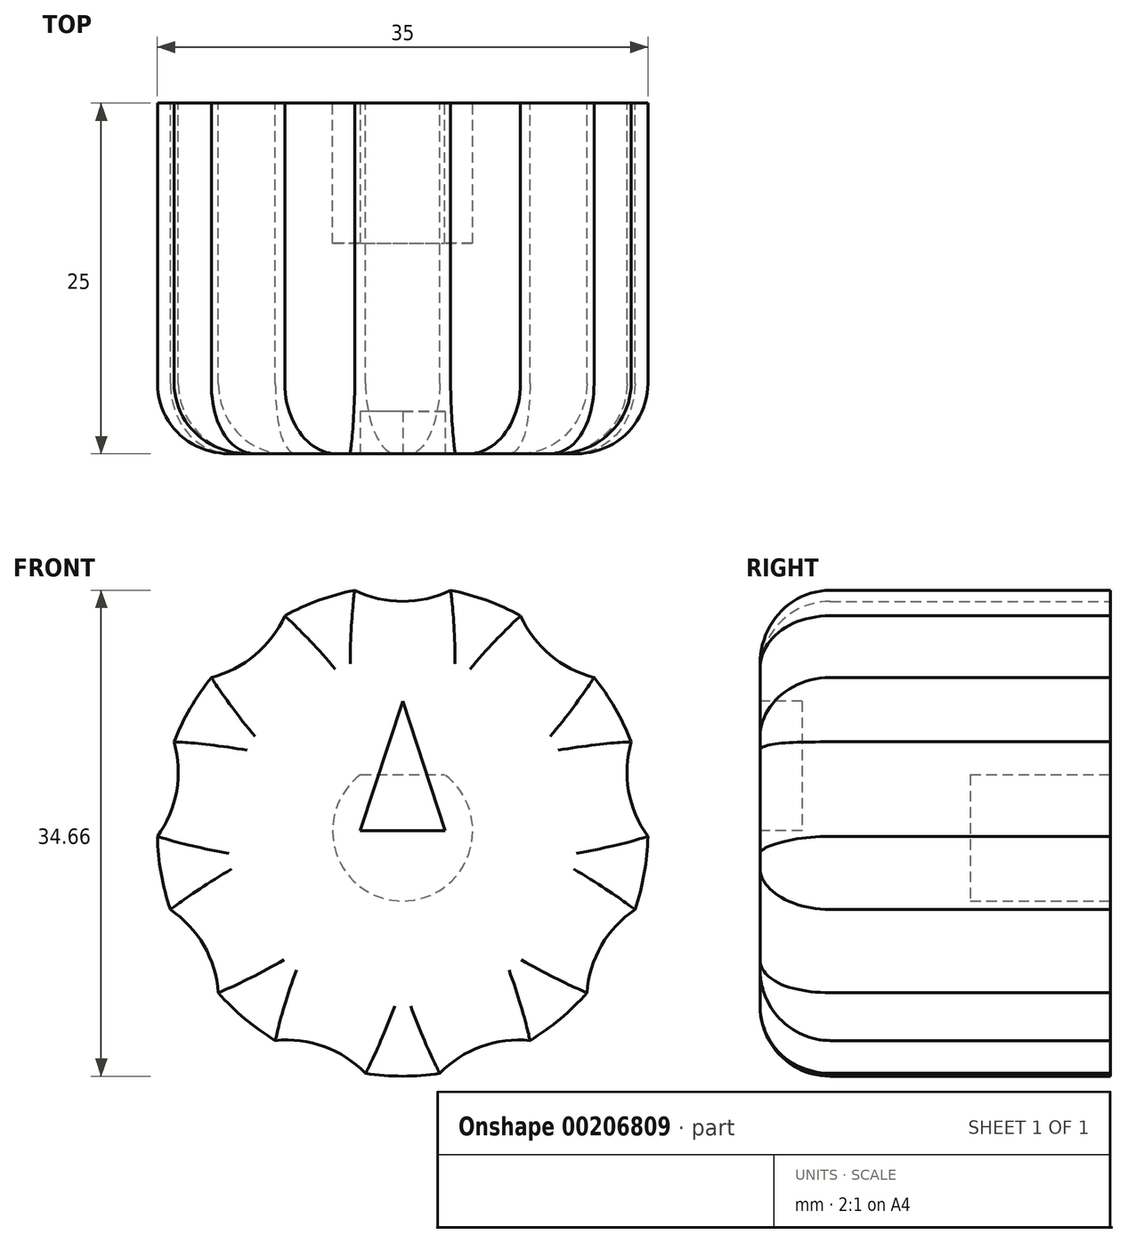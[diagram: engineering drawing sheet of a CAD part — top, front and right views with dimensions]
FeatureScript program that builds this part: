
annotation { "Feature Type Name" : "Feature", "Feature Type Description" : "" }
export const myFeature = defineFeature(function(context is Context, id is Id, definition is map)
    precondition{}
    {
        {
            var Q0;
            Q0=qCreatedBy(makeId("Front.planeOp"),FACE);
            var sketch = newSketch(context, id + "F0", { "sketchPlane" : qUnion([Q0])});
            skCircle(sketch, "E0", {"center": v(0, 0) * mm, "radius": 17.5 * mm});
            skCircle(sketch, "E1", {"center": v(0, 0) * mm, "radius": 5 * mm});
            skLineSegment(sketch, "E2", {"start": v(-3, 4) * mm, "end": v(3, 4) * mm});
            skArc(sketch, "E3", {"start": v(-3.42, 17.16) * mm, "mid": v(0, 16.37) * mm, "end": v(3.42, 17.16) * mm});
            skArc(sketch, "E4.1.0", {"start": v(-13.65, 10.95) * mm, "mid": v(-10.52, 12.54) * mm, "end": v(-8.41, 15.35) * mm});
            skArc(sketch, "E4.2.0", {"start": v(-17.5, -0.39) * mm, "mid": v(-16.12, 2.84) * mm, "end": v(-16.3, 6.35) * mm});
            skArc(sketch, "E4.3.0", {"start": v(-13.15, -11.54) * mm, "mid": v(-14.18, -8.19) * mm, "end": v(-16.57, -5.62) * mm});
            skArc(sketch, "E4.4.0", {"start": v(-2.65, -17.3) * mm, "mid": v(-5.6, -15.38) * mm, "end": v(-9.09, -14.96) * mm});
            skArc(sketch, "E4.5.0", {"start": v(9.09, -14.96) * mm, "mid": v(5.6, -15.38) * mm, "end": v(2.65, -17.3) * mm});
            skArc(sketch, "E4.6.0", {"start": v(16.57, -5.62) * mm, "mid": v(14.18, -8.19) * mm, "end": v(13.15, -11.54) * mm});
            skArc(sketch, "E4.7.0", {"start": v(16.3, 6.35) * mm, "mid": v(16.12, 2.84) * mm, "end": v(17.5, -0.39) * mm});
            skArc(sketch, "E4.8.0", {"start": v(8.41, 15.35) * mm, "mid": v(10.52, 12.54) * mm, "end": v(13.65, 10.95) * mm});
            skSolve(sketch);
        }
        {
            var Q0;
            {var subQ7=sQuery(id+"F0.wireOp",EDGE,"E3");Q0=makeQuery(id+"F0.imprint","IMPRINT",FACE,{"disambiguationData":[TD([[makeQuery(id+"F0.imprint","IMPRINT",EDGE,{"derivedFrom":subQ7}),-1.0]])]});}
            var Q1;
            {var subQ0=sQuery(id+"F0.wireOp",EDGE,"E2");Q1=makeQuery(id+"F0.imprint","IMPRINT",FACE,{"disambiguationData":[TD([[makeQuery(id+"F0.imprint","IMPRINT",EDGE,{"derivedFrom":subQ0}),1.0]])]});}
            var Q2;
            {var subQ0=sQuery(id+"F0.wireOp",EDGE,"E2");Q2=makeQuery(id+"F0.imprint","IMPRINT",FACE,{"disambiguationData":[TD([[makeQuery(id+"F0.imprint","IMPRINT",EDGE,{"derivedFrom":subQ0}),-1.0]])]});}
            extrude(context, id + "F1", {"entities" : qUnion([Q0, Q1, Q2]), "depth" : 25 * mm});
        }
        {
            var Q0;
            {var subQ0=sQuery(id+"F0.wireOp",EDGE,"E2");Q0=makeQuery(id+"F0.imprint","IMPRINT",FACE,{"disambiguationData":[TD([[makeQuery(id+"F0.imprint","IMPRINT",EDGE,{"derivedFrom":subQ0}),-1.0]])]});}
            extrude(context, id + "F2", {"entities" : qUnion([Q0]), "operationType" : NewBodyOperationType.REMOVE, "depth" : 10 * mm});
        }
        {
            var Q0;
            Q0=makeQuery(id+"F1.opExtrude","CAP_FACE",FACE,{"disambiguationData":[OSD([sQuery(id+"F0.wireOp",EDGE,"E0"),sQuery(id+"F0.wireOp",EDGE,"E3"),sQuery(id+"F0.wireOp",EDGE,"E4.1.0"),sQuery(id+"F0.wireOp",EDGE,"E4.2.0"),sQuery(id+"F0.wireOp",EDGE,"E4.3.0"),sQuery(id+"F0.wireOp",EDGE,"E4.4.0"),sQuery(id+"F0.wireOp",EDGE,"E4.5.0"),sQuery(id+"F0.wireOp",EDGE,"E4.6.0"),sQuery(id+"F0.wireOp",EDGE,"E4.7.0"),sQuery(id+"F0.wireOp",EDGE,"E4.8.0")])],"isStart":false});
            fillet(context, id + "F3", {"entities" : qUnion([Q0]), "radius" : 5 * mm, "tangentPropagation" : true, "allowEdgeOverflow" : false});
        }
        {
            var Q0;
            Q0=makeQuery(id+"F1.opExtrude","CAP_FACE",FACE,{"disambiguationData":[OSD([sQuery(id+"F0.wireOp",EDGE,"E0"),sQuery(id+"F0.wireOp",EDGE,"E3"),sQuery(id+"F0.wireOp",EDGE,"E4.1.0"),sQuery(id+"F0.wireOp",EDGE,"E4.2.0"),sQuery(id+"F0.wireOp",EDGE,"E4.3.0"),sQuery(id+"F0.wireOp",EDGE,"E4.4.0"),sQuery(id+"F0.wireOp",EDGE,"E4.5.0"),sQuery(id+"F0.wireOp",EDGE,"E4.6.0"),sQuery(id+"F0.wireOp",EDGE,"E4.7.0"),sQuery(id+"F0.wireOp",EDGE,"E4.8.0")])],"isStart":false});
            var sketch = newSketch(context, id + "F4", { "sketchPlane" : qUnion([Q0])});
            skLineSegment(sketch, "E5", {"start": v(0, 9.24) * mm, "end": v(-3.03, 0) * mm});
            skLineSegment(sketch, "E6", {"start": v(-3.03, 0) * mm, "end": v(0, 0) * mm});
            skLineSegment(sketch, "E7", {"start": v(0, 0) * mm, "end": v(0, 9.24) * mm});
            skLineSegment(sketch, "E8.MirrorCS", {"start": v(0, 9.24) * mm, "end": v(3.03, 0) * mm});
            skLineSegment(sketch, "E9.MirrorCS", {"start": v(3.03, 0) * mm, "end": v(0, 0) * mm});
            skSolve(sketch);
        }
        {
            var Q0;
            Q0=makeQuery(id+"F4.imprint","IMPRINT",FACE,{"disambiguationData":[TD([[makeQuery(id+"F4.imprint","IMPRINT",EDGE,{"derivedFrom":sQuery(id+"F4.wireOp",EDGE,"E7")}),-1.0]])]});
            var Q1;
            Q1=makeQuery(id+"F4.imprint","IMPRINT",FACE,{"disambiguationData":[TD([[makeQuery(id+"F4.imprint","IMPRINT",EDGE,{"derivedFrom":sQuery(id+"F4.wireOp",EDGE,"E5")}),1.0]])]});
            extrude(context, id + "F5", {"entities" : qUnion([Q0, Q1]), "operationType" : NewBodyOperationType.REMOVE, "oppositeDirection" : true, "depth" : 3 * mm});
        }
    });
